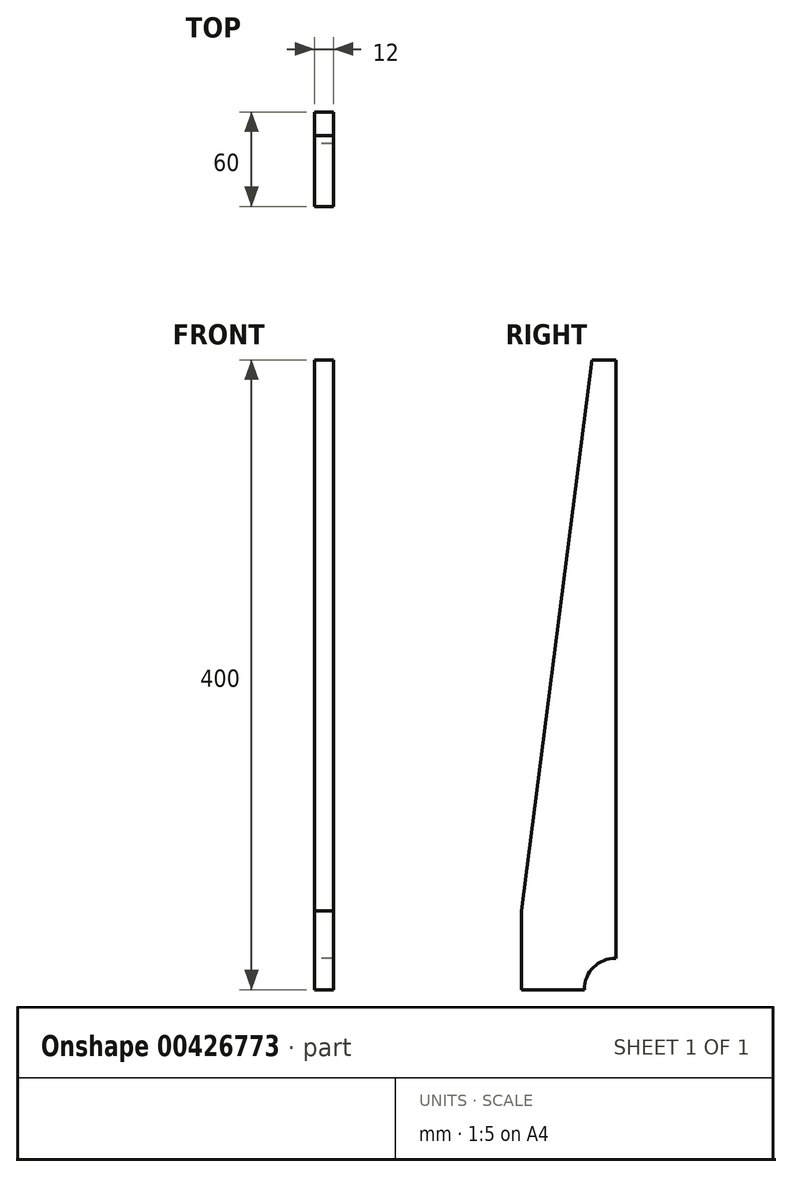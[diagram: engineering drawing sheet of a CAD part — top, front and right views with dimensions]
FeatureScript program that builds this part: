
annotation { "Feature Type Name" : "Feature", "Feature Type Description" : "" }
export const myFeature = defineFeature(function(context is Context, id is Id, definition is map)
    precondition{}
    {
        {
            var Q0;
            Q0=qCreatedBy(makeId("Right.planeOp"),FACE);
            var sketch = newSketch(context, id + "F0", { "sketchPlane" : qUnion([Q0])});
            skLineSegment(sketch, "E0.top", {"start": v(-60, 0) * mm, "end": v(-20, 0) * mm});
            skLineSegment(sketch, "E0.left", {"start": v(-60, 50) * mm, "end": v(-60, 0) * mm});
            skArc(sketch, "E1", {"start": v(0, 20) * mm, "mid": v(-14.14, 14.14) * mm, "end": v(-20, 0) * mm});
            skLineSegment(sketch, "E2", {"start": v(0, 20) * mm, "end": v(0, 400) * mm});
            skLineSegment(sketch, "E3", {"start": v(0, 400) * mm, "end": v(-15, 400) * mm});
            skLineSegment(sketch, "E4", {"start": v(-15, 400) * mm, "end": v(-60, 50) * mm});
            skSolve(sketch);
        }
        {
            var Q0;
            Q0=makeQuery(id+"F0.imprint","IMPRINT",FACE,{"disambiguationData":[TD([[makeQuery(id+"F0.imprint","IMPRINT",EDGE,{"derivedFrom":sQuery(id+"F0.wireOp",EDGE,"E0.top")}),1.0]])]});
            extrude(context, id + "F1", {"entities" : qUnion([Q0]), "depth" : 12 * mm});
        }
    });
